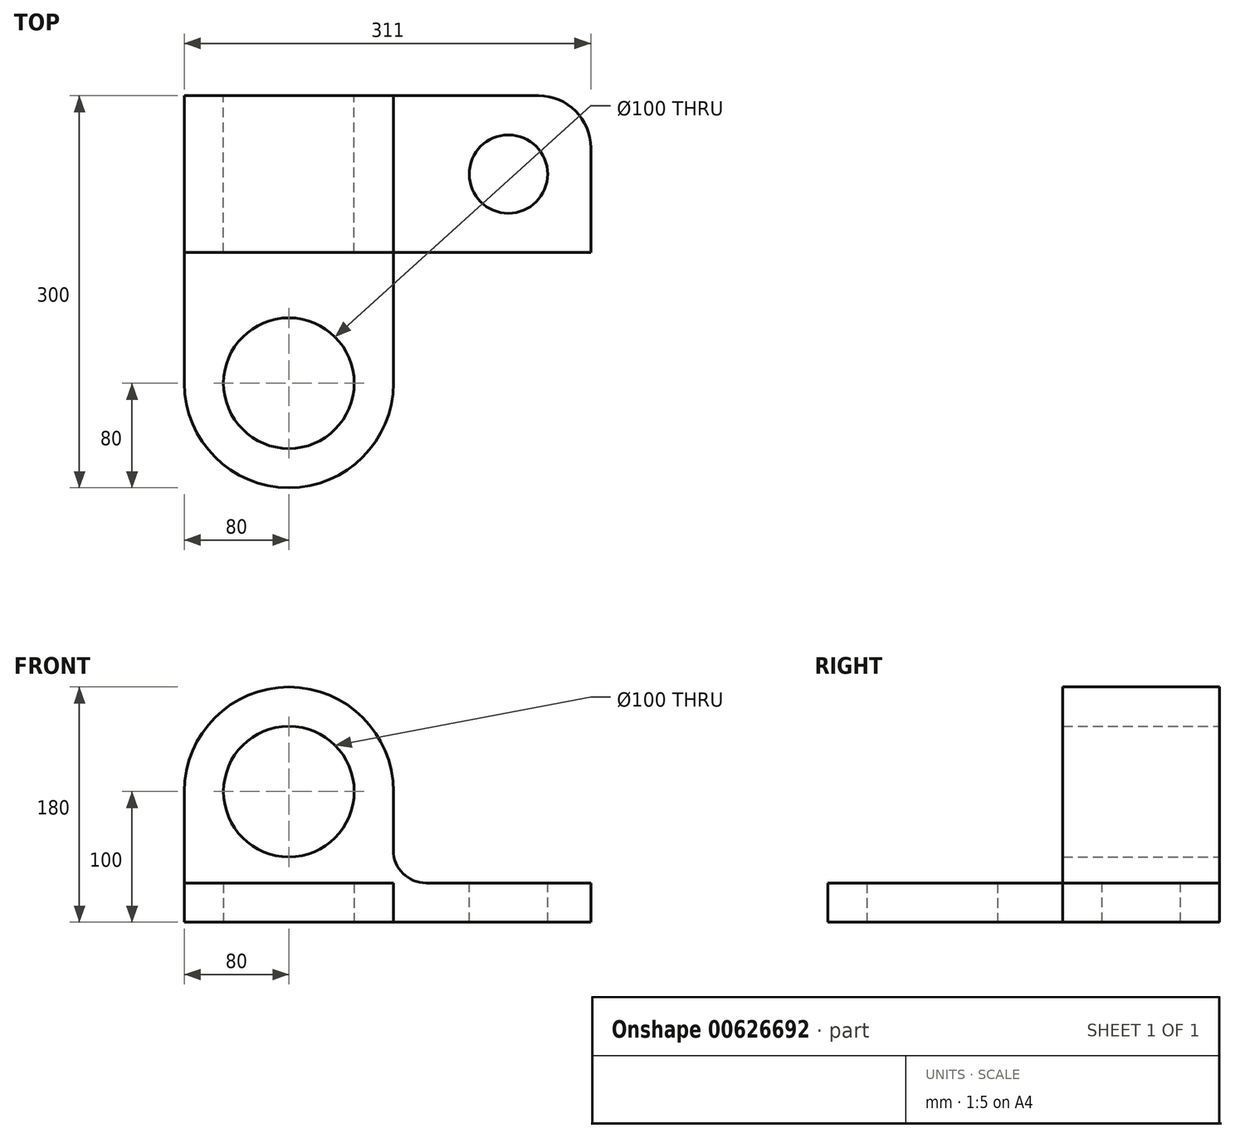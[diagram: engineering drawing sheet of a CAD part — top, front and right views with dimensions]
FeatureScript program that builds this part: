
annotation { "Feature Type Name" : "Feature", "Feature Type Description" : "" }
export const myFeature = defineFeature(function(context is Context, id is Id, definition is map)
    precondition{}
    {
        {
            var Q0;
            Q0=qCreatedBy(makeId("Front.planeOp"),FACE);
            var sketch = newSketch(context, id + "F0", { "sketchPlane" : qUnion([Q0])});
            skLineSegment(sketch, "E0.top", {"start": v(0, 0) * mm, "end": v(311, 0) * mm});
            skLineSegment(sketch, "E0.left", {"start": v(0, 100) * mm, "end": v(0, 0) * mm});
            skLineSegment(sketch, "E0.right", {"start": v(311, 30) * mm, "end": v(311, 0) * mm});
            skLineSegment(sketch, "E1", {"start": v(311, 30) * mm, "end": v(185, 30) * mm});
            skPoint(sketch, "E2", {"position": v(80, 100) * mm});
            skArc(sketch, "E3", {"start": v(160, 100) * mm, "mid": v(80, 180) * mm, "end": v(0, 100) * mm});
            skLineSegment(sketch, "E4", {"start": v(160, 100) * mm, "end": v(160, 55) * mm});
            skPoint(sketch, "E5", {"position": v(185, 55) * mm});
            skArc(sketch, "E6", {"start": v(160, 55) * mm, "mid": v(167.32, 37.32) * mm, "end": v(185, 30) * mm});
            skCircle(sketch, "E7", {"center": v(80, 100) * mm, "radius": 50 * mm});
            skSolve(sketch);
        }
        {
            var Q0;
            Q0 = qSketchRegion(id + "F0", true);
            extrude(context, id + "F1", {"entities" : qUnion([Q0]), "depth" : 120 * mm, "offsetDistance" : 25 * mm});
        }
        {
            var Q0;
            Q0=makeQuery(id+"F1.opExtrude","SWEPT_FACE",FACE,{"disambiguationData":[OSD([sQuery(id+"F0.wireOp",EDGE,"E1")])]});
            var sketch = newSketch(context, id + "F2", { "sketchPlane" : qUnion([Q0])});
            skPoint(sketch, "E8", {"position": v(248, -60) * mm});
            skCircle(sketch, "E9", {"center": v(248, -60) * mm, "radius": 30 * mm});
            skPoint(sketch, "E10", {"position": v(271, -40) * mm});
            skLineSegment(sketch, "E11", {"start": v(271, 0) * mm, "end": v(311, 0) * mm});
            skLineSegment(sketch, "E12", {"start": v(311, 0) * mm, "end": v(311, -40) * mm});
            skArc(sketch, "E13.trimOffspring", {"start": v(311, -40) * mm, "mid": v(299.28, -11.72) * mm, "end": v(271, 0) * mm});
            skSolve(sketch);
        }
        {
            var Q0;
            Q0 = qSketchRegion(id + "F2", true);
            extrude(context, id + "F3", {"entities" : qUnion([Q0]), "operationType" : NewBodyOperationType.REMOVE, "oppositeDirection" : true, "depth" : 30 * mm, "offsetDistance" : 25 * mm});
        }
        {
            var Q0;
            Q0=makeQuery(id+"F1.opExtrude","SWEPT_FACE",FACE,{"disambiguationData":[OSD([sQuery(id+"F0.wireOp",EDGE,"E0.top")])]});
            var sketch = newSketch(context, id + "F4", { "sketchPlane" : qUnion([Q0])});
            skLineSegment(sketch, "E14.bottom", {"start": v(0, 120) * mm, "end": v(160, 120) * mm});
            skLineSegment(sketch, "E14.left", {"start": v(0, 120) * mm, "end": v(0, 220) * mm});
            skLineSegment(sketch, "E14.right", {"start": v(160, 120) * mm, "end": v(160, 220) * mm});
            skPoint(sketch, "E15", {"position": v(80, 220) * mm});
            skArc(sketch, "E16", {"start": v(160, 220) * mm, "mid": v(80, 300) * mm, "end": v(0, 220) * mm});
            skCircle(sketch, "E17", {"center": v(80, 220) * mm, "radius": 50 * mm});
            skSolve(sketch);
        }
        {
            var Q0;
            Q0 = qSketchRegion(id + "F4", true);
            extrude(context, id + "F5", {"entities" : qUnion([Q0]), "operationType" : NewBodyOperationType.ADD, "oppositeDirection" : true, "depth" : 30 * mm, "offsetDistance" : 25 * mm});
        }
    });
